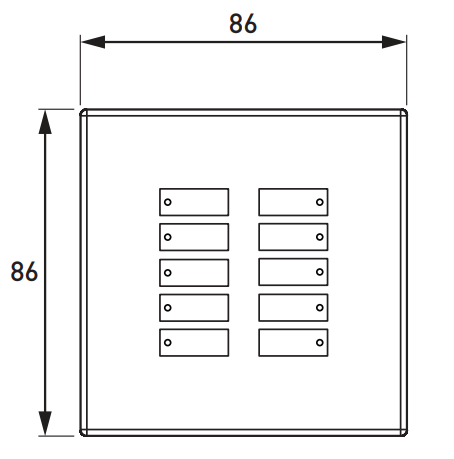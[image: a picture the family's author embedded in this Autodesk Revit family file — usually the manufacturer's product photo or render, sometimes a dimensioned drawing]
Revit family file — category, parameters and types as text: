
# Revit family: Enocean Panel _182X
name_source: partatom
category: Electrical Fixtures
revit_build: Autodesk Revit 2018 (Build: 20170223_1515(x64)
units: mm (PartAtom-declared; Revit-internal decimal feet)

## family parameters
Always vertical = Yes
Cut with Voids When Loaded = No
Maintain Annotation Orientation = No
Part Type = Normal
Room Calculation Point = No
Round Connector Dimension = Use Diameter
Shared = No
Work Plane-Based = Yes

## types (1)
- Dual Rocker Switch_Black/White
    Ambient temperature = 0 °C to +50 °C
    Connections = No wiring (power or communications) is required
    Default Elevation = 0 mm  [stored 0 ft]
    Dimensions = 86 mm × 86 mm × 15 mm
    Environment = Complies with WEEE and RoHS directives.
    Frame = Stainless steel
    IP code = IP30
    Manufacturer = Helvar
    Material: = Switch rockers: plastic
    Max. No. of switch panels per gateway = 20
    Model = 182B/182W
    Mounting = Mount to back box, or mount on glass or flat surface
    Operating frequency = 868 MHz ISM band (Europe)
    Power = Signal power is generated by pressing the EnOcean button.
    RED 2014/53/EU = EN 301489-3, EN 300220-2
    Range: = 30 m (unobstructed space)
    Relative humidity = Max. 90 %, noncondensing
    Safety = EN 60950-1
    Storage temperature = –10 °C to +70 °C
    Switch colour = 18xW: white 18xB: black
    Weight = 150 g
    Wireless protocol = ISO/IEC 14543–3–10

note: [stored X ft] marks values corroborated as IEEE doubles in the binary element streams (Revit-internal decimal feet)

## geometry (parser evidence)
native form markers: Sweep x15
no freeform markers — native parametric forms only
